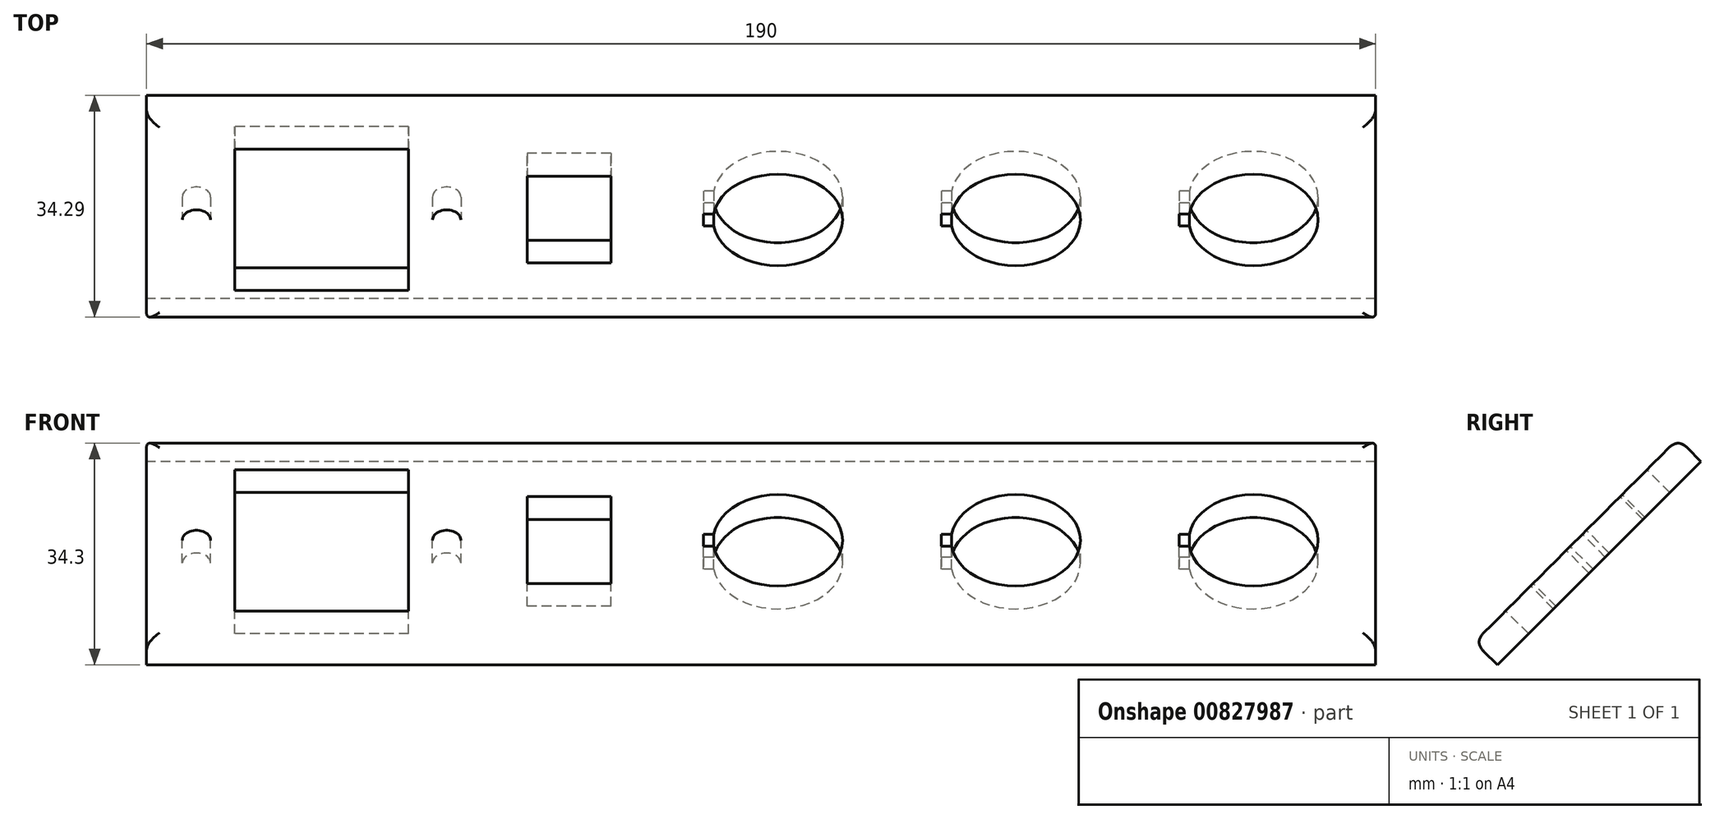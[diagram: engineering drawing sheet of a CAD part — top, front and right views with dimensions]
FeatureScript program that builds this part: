
annotation { "Feature Type Name" : "Feature", "Feature Type Description" : "" }
export const myFeature = defineFeature(function(context is Context, id is Id, definition is map)
    precondition{}
    {
        {
            var Q0;
            Q0=qCreatedBy(makeId("Top.planeOp"),FACE);
            var sketch = newSketch(context, id + "F0", { "sketchPlane" : qUnion([Q0])});
            skLineSegment(sketch, "E0.bottom", {"start": v(95, -22.25) * mm, "end": v(-95, -22.25) * mm});
            skLineSegment(sketch, "E0.top", {"start": v(95, 22.25) * mm, "end": v(-95, 22.25) * mm});
            skLineSegment(sketch, "E0.left", {"start": v(95, -22.25) * mm, "end": v(95, 22.25) * mm});
            skLineSegment(sketch, "E0.right", {"start": v(-95, -22.25) * mm, "end": v(-95, 22.25) * mm});
            skPoint(sketch, "E0.middle", {"position": v(0, 0) * mm});
            skSolve(sketch);
        }
        {
            var Q0;
            Q0 = qSketchRegion(id + "F0", true);
            extrude(context, id + "F1", {"entities" : qUnion([Q0]), "depth" : 5 * mm, "offsetDistance" : 25 * mm});
        }
        {
            var Q0;
            Q0=makeQuery(id+"F1.opExtrude","CAP_FACE",FACE,{"disambiguationData":[OSD([sQuery(id+"F0.wireOp",EDGE,"E0.bottom"),sQuery(id+"F0.wireOp",EDGE,"E0.top"),sQuery(id+"F0.wireOp",EDGE,"E0.left"),sQuery(id+"F0.wireOp",EDGE,"E0.right")])],"isStart":false});
            var sketch = newSketch(context, id + "F2", { "sketchPlane" : qUnion([Q0])});
            skLineSegment(sketch, "E1.bottom", {"start": v(-54.5, -15.43) * mm, "end": v(-81.38, -15.43) * mm});
            skLineSegment(sketch, "E1.top", {"start": v(-54.5, 15.43) * mm, "end": v(-81.38, 15.43) * mm});
            skLineSegment(sketch, "E1.left", {"start": v(-54.5, -15.43) * mm, "end": v(-54.5, 15.43) * mm});
            skLineSegment(sketch, "E1.right", {"start": v(-81.38, -15.43) * mm, "end": v(-81.38, 15.43) * mm});
            skLineSegment(sketch, "E2.bottom", {"start": v(-23.21, -9.44) * mm, "end": v(-36.16, -9.44) * mm});
            skLineSegment(sketch, "E2.top", {"start": v(-23.21, 9.56) * mm, "end": v(-36.16, 9.56) * mm});
            skLineSegment(sketch, "E2.left", {"start": v(-23.21, -9.44) * mm, "end": v(-23.21, 9.56) * mm});
            skLineSegment(sketch, "E2.right", {"start": v(-36.16, -9.44) * mm, "end": v(-36.16, 9.56) * mm});
            skPoint(sketch, "E3", {"position": v(-48.6, 0) * mm});
            skPoint(sketch, "E4.endSnap0", {"position": v(-67.93, -15.43) * mm});
            skPoint(sketch, "E5.MirrorP", {"position": v(-87.28, 0) * mm});
            skArc(sketch, "E6", {"start": v(-7.31, -1.32) * mm, "mid": v(12.6, 0) * mm, "end": v(-7.31, 1.33) * mm});
            skLineSegment(sketch, "E7.top", {"start": v(-7.31, -1.32) * mm, "end": v(-8.9, -1.32) * mm});
            skLineSegment(sketch, "E8.MirrorCS", {"start": v(-7.31, 1.33) * mm, "end": v(-8.9, 1.33) * mm});
            skPoint(sketch, "E9.orphan", {"position": v(-7.31, 1.33) * mm});
            skPoint(sketch, "E10.orphan", {"position": v(-8.9, 1.33) * mm});
            skPoint(sketch, "E7.right.start.orphan", {"position": v(-8.9, 0) * mm});
            skLineSegment(sketch, "E11", {"start": v(-8.9, 1.33) * mm, "end": v(-8.9, -1.32) * mm});
            skArc(sketch, "E12", {"start": v(29.44, -1.32) * mm, "mid": v(49.35, 0) * mm, "end": v(29.44, 1.33) * mm});
            skLineSegment(sketch, "E13.top", {"start": v(29.44, -1.32) * mm, "end": v(27.85, -1.32) * mm});
            skLineSegment(sketch, "E14.MirrorCS", {"start": v(29.44, 1.33) * mm, "end": v(27.85, 1.33) * mm});
            skLineSegment(sketch, "E15", {"start": v(27.85, 1.33) * mm, "end": v(27.85, -1.32) * mm});
            skArc(sketch, "E16", {"start": v(66.2, -1.33) * mm, "mid": v(86.1, 0) * mm, "end": v(66.2, 1.32) * mm});
            skLineSegment(sketch, "E17.top", {"start": v(66.2, -1.33) * mm, "end": v(64.6, -1.33) * mm});
            skLineSegment(sketch, "E18.MirrorCS", {"start": v(66.2, 1.32) * mm, "end": v(64.6, 1.32) * mm});
            skLineSegment(sketch, "E19", {"start": v(64.6, 1.32) * mm, "end": v(64.6, -1.33) * mm});
            skSolve(sketch);
        }
        {
            var Q0;
            Q0=makeQuery(id+"F2.imprint","IMPRINT",FACE,{"disambiguationData":[TD([[makeQuery(id+"F2.imprint","IMPRINT",EDGE,{"derivedFrom":sQuery(id+"F2.wireOp",EDGE,"E1.bottom")}),-1.0]])]});
            var Q1;
            Q1=makeQuery(id+"F2.imprint","IMPRINT",FACE,{"disambiguationData":[TD([[makeQuery(id+"F2.imprint","IMPRINT",EDGE,{"derivedFrom":sQuery(id+"F2.wireOp",EDGE,"E2.bottom")}),-1.0]])]});
            var Q2;
            Q2=makeQuery(id+"F2.imprint","IMPRINT",FACE,{"disambiguationData":[TD([[makeQuery(id+"F2.imprint","IMPRINT",EDGE,{"derivedFrom":sQuery(id+"F2.wireOp",EDGE,"E6")}),1.0]])]});
            var Q3;
            Q3=makeQuery(id+"F2.imprint","IMPRINT",FACE,{"disambiguationData":[TD([[makeQuery(id+"F2.imprint","IMPRINT",EDGE,{"derivedFrom":sQuery(id+"F2.wireOp",EDGE,"E12")}),1.0]])]});
            var Q4;
            Q4=makeQuery(id+"F2.imprint","IMPRINT",FACE,{"disambiguationData":[TD([[makeQuery(id+"F2.imprint","IMPRINT",EDGE,{"derivedFrom":sQuery(id+"F2.wireOp",EDGE,"E16")}),1.0]])]});
            extrude(context, id + "F3", {"entities" : qUnion([Q0, Q1, Q2, Q3, Q4]), "operationType" : NewBodyOperationType.REMOVE, "endBound" : BoundingType.THROUGH_ALL, "oppositeDirection" : true, "depth" : 25 * mm, "offsetDistance" : 25 * mm});
        }
        {
            var Q0;
            Q0=sQuery(id+"F2.wireOp",VERTEX,"E5.MirrorP");
            var Q1;
            Q1=sQuery(id+"F2.wireOp",VERTEX,"E3");
            var Q2;
            Q2=makeQuery(id+"F1.opExtrude","SWEPT_BODY",BODY,{"disambiguationData":[OSD([sQuery(id+"F0.wireOp",EDGE,"E0.bottom"),sQuery(id+"F0.wireOp",EDGE,"E0.top"),sQuery(id+"F0.wireOp",EDGE,"E0.left"),sQuery(id+"F0.wireOp",EDGE,"E0.right")])]});
            hole(context, id + "F4", {"style" : HoleStyle.SIMPLE, "endStyle" : HoleEndStyle.THROUGH, "standardTappedOrClearance" : lookupTablePath({ "fit" : "Normal", "standard" : "ISO", "size" : "M4", "type" : "Clearance" }), "standardBlindInLast" : lookupTablePath({ "fit" : "Standard", "standard" : "ISO", "size" : "M4", "type" : "Clearance" }), "holeDiameter" : 4.4 * mm, "majorDiameter" : 5 * mm, "isTappedThrough" : true, "tappedDepth" : 12 * mm, "tapClearance" : 3, "locations" : qUnion([Q0, Q1]), "scope" : qUnion([Q2])});
        }
        {
            var Q0;
            Q0=makeQuery(id+"F1.opExtrude","SWEPT_BODY",BODY,{"disambiguationData":[OSD([sQuery(id+"F0.wireOp",EDGE,"E0.bottom"),sQuery(id+"F0.wireOp",EDGE,"E0.top"),sQuery(id+"F0.wireOp",EDGE,"E0.left"),sQuery(id+"F0.wireOp",EDGE,"E0.right")])]});
            var Q1;
            Q1=makeQuery(id+"F1.opExtrude","CAP_EDGE",EDGE,{"disambiguationData":[OSD([sQuery(id+"F0.wireOp",EDGE,"E0.bottom")])],"isStart":false});
            transform(context, id + "F5", {"entities" : qUnion([Q0]), "transformType" : TransformType.ROTATION, "transformAxis" : qUnion([Q1]), "angle" : 45 * degree, "oppositeDirection" : true, "makeCopy" : false});
        }
        {
            var Q0;
            Q0=makeQuery(id+"F1.opExtrude","CAP_EDGE",EDGE,{"disambiguationData":[OSD([sQuery(id+"F0.wireOp",EDGE,"E0.right")])],"isStart":false});
            var Q1;
            Q1=makeQuery(id+"F1.opExtrude","CAP_EDGE",EDGE,{"disambiguationData":[OSD([sQuery(id+"F0.wireOp",EDGE,"E0.top")])],"isStart":false});
            var Q2;
            Q2=makeQuery(id+"F1.opExtrude","CAP_EDGE",EDGE,{"disambiguationData":[OSD([sQuery(id+"F0.wireOp",EDGE,"E0.bottom")])],"isStart":false});
            var Q3;
            Q3=makeQuery(id+"F1.opExtrude","CAP_EDGE",EDGE,{"disambiguationData":[OSD([sQuery(id+"F0.wireOp",EDGE,"E0.left")])],"isStart":false});
            fillet(context, id + "F6", {"entities" : qUnion([Q0, Q1, Q2, Q3]), "radius" : 2 * mm, "tangentPropagation" : true, "rho" : 0.5, "crossSection" : FilletCrossSection.CONIC, "allowEdgeOverflow" : false});
        }
    });
